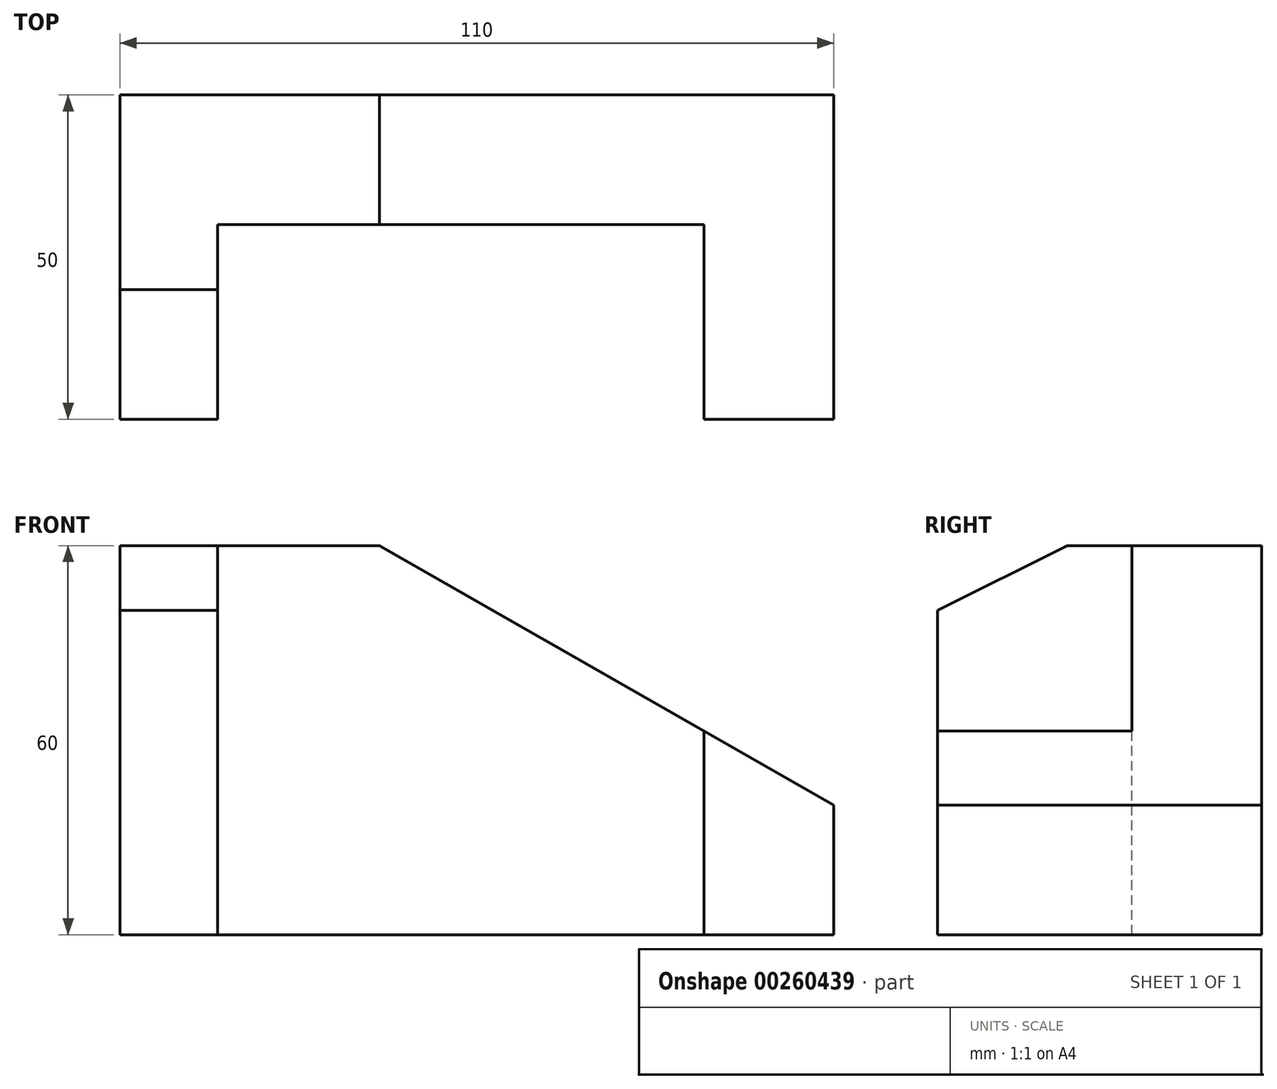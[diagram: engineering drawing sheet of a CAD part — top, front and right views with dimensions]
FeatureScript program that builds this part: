
annotation { "Feature Type Name" : "Feature", "Feature Type Description" : "" }
export const myFeature = defineFeature(function(context is Context, id is Id, definition is map)
    precondition{}
    {
        {
            assignVariable(context, id + "F0", {"name" : "B", "anyValue" : 60});
        }
        {
            assignVariable(context, id + "F1", {"name" : "C", "anyValue" : 50});
        }
        {
            var Q0;
            Q0=qCreatedBy(makeId("Top.planeOp"),FACE);
            var sketch = newSketch(context, id + "F2", { "sketchPlane" : qUnion([Q0])});
            skLineSegment(sketch, "E0.bottom", {"start": v(-55, 25) * mm, "end": v(55, 25) * mm});
            skLineSegment(sketch, "E0.top", {"start": v(-55, -25) * mm, "end": v(55, -25) * mm});
            skLineSegment(sketch, "E0.left", {"start": v(-55, 25) * mm, "end": v(-55, -25) * mm});
            skLineSegment(sketch, "E0.right", {"start": v(55, 25) * mm, "end": v(55, -25) * mm});
            skPoint(sketch, "E0.middle", {"position": v(0, 0) * mm});
            skSolve(sketch);
        }
        {
            var Q0;
            Q0 = qSketchRegion(id + "F2", true);
            extrude(context, id + "F3", {"entities" : qUnion([Q0]), "depth" : (getVariable(context, 'B')) * mm});
        }
        {
            var Q0;
            Q0=makeQuery(id+"F3.opExtrude","CAP_FACE",FACE,{"disambiguationData":[OSD([sQuery(id+"F2.wireOp",EDGE,"E0.bottom"),sQuery(id+"F2.wireOp",EDGE,"E0.top"),sQuery(id+"F2.wireOp",EDGE,"E0.left"),sQuery(id+"F2.wireOp",EDGE,"E0.right")])],"isStart":false});
            var sketch = newSketch(context, id + "F4", { "sketchPlane" : qUnion([Q0])});
            skLineSegment(sketch, "E1.bottom", {"start": v(-40, -25) * mm, "end": v(35, -25) * mm});
            skLineSegment(sketch, "E1.top", {"start": v(-40, 5) * mm, "end": v(35, 5) * mm});
            skLineSegment(sketch, "E1.left", {"start": v(-40, -25) * mm, "end": v(-40, 5) * mm});
            skLineSegment(sketch, "E1.right", {"start": v(35, -25) * mm, "end": v(35, 5) * mm});
            skSolve(sketch);
        }
        {
            var Q0;
            Q0 = qSketchRegion(id + "F4", true);
            extrude(context, id + "F5", {"entities" : qUnion([Q0]), "operationType" : NewBodyOperationType.REMOVE, "oppositeDirection" : true, "depth" : (getVariable(context, 'B')) * mm});
        }
        {
            var Q0;
            Q0=makeQuery(id+"F3.opExtrude","SWEPT_FACE",FACE,{"disambiguationData":[OSD([sQuery(id+"F2.wireOp",EDGE,"E0.bottom")])]});
            var sketch = newSketch(context, id + "F6", { "sketchPlane" : qUnion([Q0])});
            skLineSegment(sketch, "E2.bottom", {"start": v(-55, 60) * mm, "end": v(15, 60) * mm});
            skLineSegment(sketch, "E2.left", {"start": v(-55, 60) * mm, "end": v(-55, 20) * mm});
            skLineSegment(sketch, "E3", {"start": v(-55, 20) * mm, "end": v(15, 60) * mm});
            skSolve(sketch);
        }
        {
            var Q0;
            Q0 = qSketchRegion(id + "F6", true);
            extrude(context, id + "F7", {"entities" : qUnion([Q0]), "operationType" : NewBodyOperationType.REMOVE, "oppositeDirection" : true, "depth" : (getVariable(context, 'C')) * mm});
        }
        {
            var Q0;
            Q0=makeQuery(id+"F5.boolean.opBoolean","COPY",FACE,{"derivedFrom":makeQuery(id+"F5.opExtrude","SWEPT_FACE",FACE,{"disambiguationData":[OSD([sQuery(id+"F4.wireOp",EDGE,"E1.left")])]})});
            var sketch = newSketch(context, id + "F8", { "sketchPlane" : qUnion([Q0])});
            skLineSegment(sketch, "E4.bottom", {"start": v(-25, 60) * mm, "end": v(-5, 60) * mm});
            skLineSegment(sketch, "E4.left", {"start": v(-25, 60) * mm, "end": v(-25, 50) * mm});
            skLineSegment(sketch, "E5", {"start": v(-25, 50) * mm, "end": v(-5, 60) * mm});
            skSolve(sketch);
        }
        {
            var Q0;
            Q0 = qSketchRegion(id + "F8", true);
            extrude(context, id + "F9", {"entities" : qUnion([Q0]), "operationType" : NewBodyOperationType.REMOVE, "oppositeDirection" : true, "depth" : 15 * mm});
        }
    });
